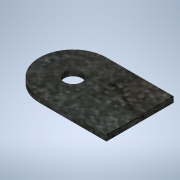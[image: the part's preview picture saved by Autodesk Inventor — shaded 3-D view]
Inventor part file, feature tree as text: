
AUTODESK INVENTOR PART (.ipt)
format: ipt  version: 2021 (Build 250183000, 183)  size: 128,512 bytes
history: native  units: in
note: dims shown in document units (in); Inventor stores cm internally (conversion verified against a paired STEP export)
features: other x2, extrude x2, sketch x2
ambient origin geometry x8: Origin, YZ Plane, XZ Plane, XY Plane, X Axis, Y Axis, Z Axis, Center Point
bodies: Solid1 (feature_tree)
feature tree (6):
  other  "Annotations"
  extrude  "Extrusion1"  Depth=0.75in
  extrude  "Extrusion2"  Depth=0.75in
  sketch  "Sketch1"  dims[d0=0.201in d1=0.75in]
  sketch  "Sketch2"  dims[d2=0.75in d3=0.75in d4=0.0625in d5=0.0in d7=1.0in d8=2.0in d9=0.0in d10=0.0in d11=0.3937in d12=0.75in d13=0.0344in]
  other  "Linear Dimension 1"
